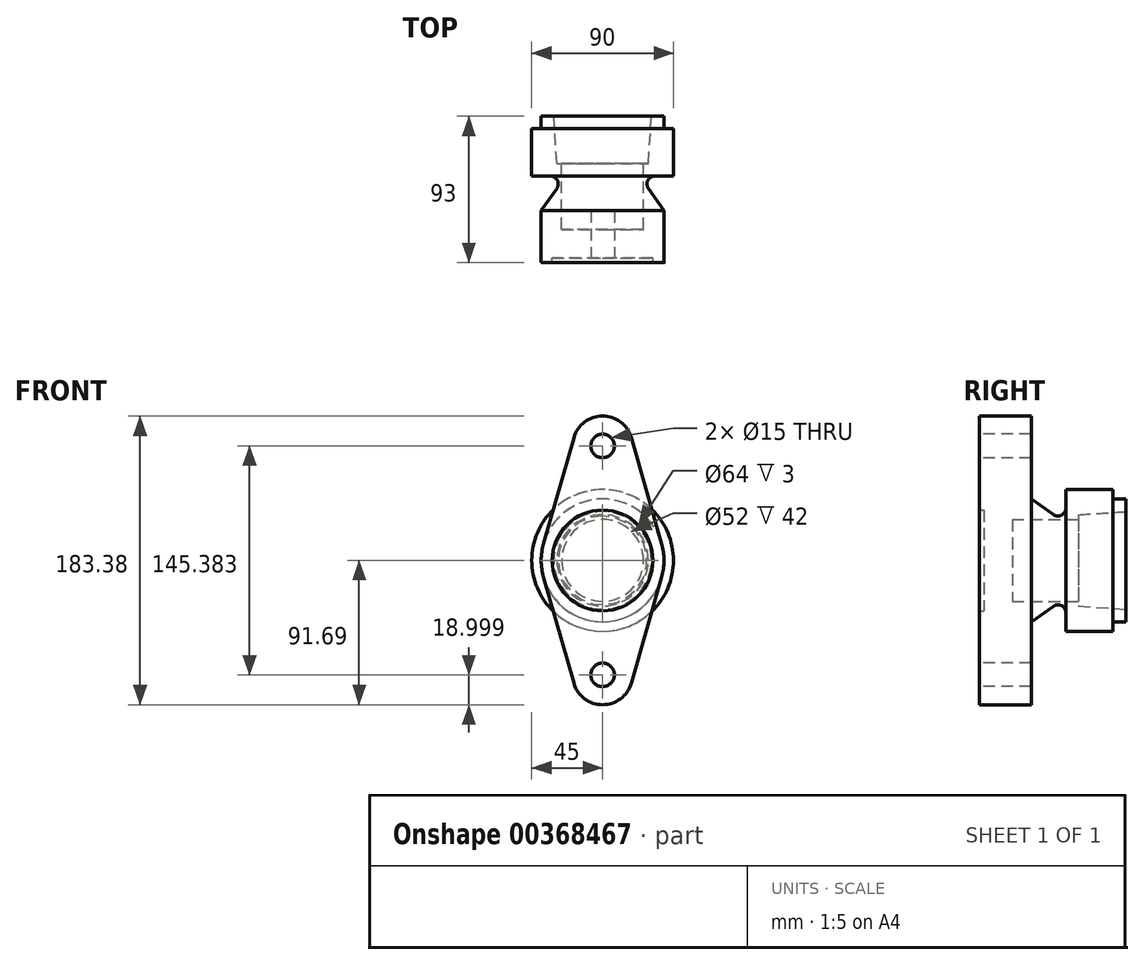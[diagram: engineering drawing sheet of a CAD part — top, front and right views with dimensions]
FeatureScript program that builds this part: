
annotation { "Feature Type Name" : "Feature", "Feature Type Description" : "" }
export const myFeature = defineFeature(function(context is Context, id is Id, definition is map)
    precondition{}
    {
        {
            var Q0;
            Q0=qCreatedBy(makeId("Right.planeOp"),FACE);
            var sketch = newSketch(context, id + "F0", { "sketchPlane" : qUnion([Q0])});
            skLineSegment(sketch, "E0", {"start": v(3, 0) * mm, "end": v(3, 32) * mm});
            skLineSegment(sketch, "E1", {"start": v(3, 32) * mm, "end": v(0, 32) * mm});
            skLineSegment(sketch, "E2", {"start": v(0, 32) * mm, "end": v(0, 39) * mm});
            skLineSegment(sketch, "E3", {"start": v(0, 39) * mm, "end": v(33, 39) * mm});
            skLineSegment(sketch, "E4", {"start": v(33, 39) * mm, "end": v(47.13, 29.1) * mm});
            skLineSegment(sketch, "E5", {"start": v(55, 33.2) * mm, "end": v(55, 45) * mm});
            skLineSegment(sketch, "E6", {"start": v(55, 45) * mm, "end": v(85, 45) * mm});
            skLineSegment(sketch, "E7", {"start": v(85, 45) * mm, "end": v(85, 39) * mm});
            skLineSegment(sketch, "E8", {"start": v(85, 39) * mm, "end": v(93, 39) * mm});
            skLineSegment(sketch, "E9", {"start": v(93, 39) * mm, "end": v(93, 31) * mm});
            skLineSegment(sketch, "E10", {"start": v(93, 31) * mm, "end": v(63, 29) * mm});
            skLineSegment(sketch, "E11", {"start": v(63, 29) * mm, "end": v(63, 26) * mm});
            skLineSegment(sketch, "E12", {"start": v(63, 26) * mm, "end": v(21, 26) * mm});
            skLineSegment(sketch, "E13", {"start": v(21, 26) * mm, "end": v(21, 0) * mm});
            skLineSegment(sketch, "E14", {"start": v(21, 0) * mm, "end": v(3, 0) * mm});
            skPoint(sketch, "E15.visualSharp", {"position": v(55, 23.6) * mm});
            skArc(sketch, "E15.filletArc", {"start": v(47.13, 29.1) * mm, "mid": v(52.3, 28.77) * mm, "end": v(55, 33.2) * mm});
            skSolve(sketch);
        }
        {
            var Q0;
            Q0=qSketchRegion(id+"F0",true);
            var Q1;
            Q1=sQuery(id+"F0.wireOp",EDGE,"E14");
            revolve(context, id + "F1", {"entities" : qUnion([Q0]), "axis" : qUnion([Q1]), "revolveType" : RevolveType.FULL});
        }
        {
            var Q0;
            Q0=qCreatedBy(makeId("Front.planeOp"),FACE);
            var sketch = newSketch(context, id + "F2", { "sketchPlane" : qUnion([Q0])});
            skLineSegment(sketch, "E16", {"start": v(0, 0) * mm, "end": v(0, 150) * mm, "construction": true});
            skLineSegment(sketch, "E17", {"start": v(0, 72.7) * mm, "end": v(70, 72.7) * mm, "construction": true});
            skLineSegment(sketch, "E18", {"start": v(0, 72.7) * mm, "end": v(-66.14, 72.7) * mm, "construction": true});
            skCircle(sketch, "E19", {"center": v(0, 72.7) * mm, "radius": 7.5 * mm});
            skArc(sketch, "E20", {"start": v(18.27, 77.92) * mm, "mid": v(0, 91.7) * mm, "end": v(-18.27, 77.92) * mm});
            skArc(sketch, "E21", {"start": v(-37.5, -10.73) * mm, "mid": v(0, -39) * mm, "end": v(37.5, -10.73) * mm});
            skPoint(sketch, "E22.end.orphan", {"position": v(-40.7, 0) * mm});
            skPoint(sketch, "E23.end.orphan", {"position": v(40.7, 0) * mm});
            skLineSegment(sketch, "E24", {"start": v(-18.27, 77.92) * mm, "end": v(-37.5, 10.73) * mm});
            skLineSegment(sketch, "E25", {"start": v(37.5, 10.73) * mm, "end": v(18.27, 77.92) * mm});
            skLineSegment(sketch, "E26.MirrorCS", {"start": v(-18.27, -77.92) * mm, "end": v(-37.5, -10.73) * mm});
            skLineSegment(sketch, "E27.MirrorCS", {"start": v(37.5, -10.73) * mm, "end": v(18.27, -77.92) * mm});
            skCircle(sketch, "E28.MirrorC", {"center": v(0, -72.7) * mm, "radius": 7.5 * mm});
            skArc(sketch, "E29.MirrorCS", {"start": v(18.27, -77.92) * mm, "mid": v(0, -91.7) * mm, "end": v(-18.27, -77.92) * mm});
            skArc(sketch, "E30.trimOffspring", {"start": v(37.5, 10.73) * mm, "mid": v(0, 39) * mm, "end": v(-37.5, 10.73) * mm});
            skSolve(sketch);
        }
        {
            var Q0;
            Q0=makeQuery(id+"F2.imprint","IMPRINT",FACE,{"disambiguationData":[TD([[makeQuery(id+"F2.imprint","IMPRINT",EDGE,{"derivedFrom":sQuery(id+"F2.wireOp",EDGE,"E19")}),-1.0]])]});
            var Q1;
            Q1=makeQuery(id+"F2.imprint","IMPRINT",FACE,{"disambiguationData":[TD([[makeQuery(id+"F2.imprint","IMPRINT",EDGE,{"derivedFrom":sQuery(id+"F2.wireOp",EDGE,"E21")}),-1.0]])]});
            extrude(context, id + "F3", {"entities" : qUnion([Q0, Q1]), "operationType" : NewBodyOperationType.ADD, "oppositeDirection" : true, "depth" : 33 * mm});
        }
    });
